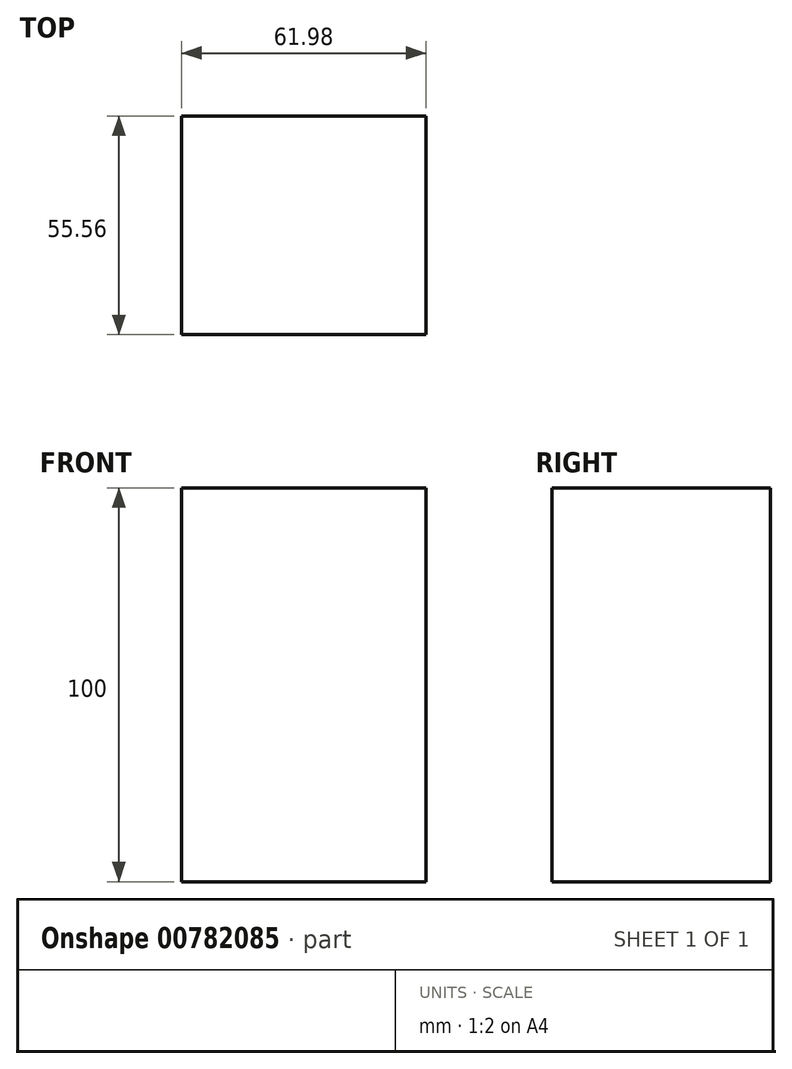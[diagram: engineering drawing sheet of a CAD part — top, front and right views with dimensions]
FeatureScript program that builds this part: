
annotation { "Feature Type Name" : "Feature", "Feature Type Description" : "" }
export const myFeature = defineFeature(function(context is Context, id is Id, definition is map)
    precondition{}
    {
        {
            var Q0;
            Q0=qCreatedBy(makeId("Top.planeOp"),FACE);
            var sketch = newSketch(context, id + "F0", { "sketchPlane" : qUnion([Q0])});
            skLineSegment(sketch, "E0.bottom", {"start": v(-31, 27.78) * mm, "end": v(31, 27.78) * mm});
            skLineSegment(sketch, "E0.top", {"start": v(-31, -27.78) * mm, "end": v(31, -27.78) * mm});
            skLineSegment(sketch, "E0.left", {"start": v(-31, 27.78) * mm, "end": v(-31, -27.78) * mm});
            skLineSegment(sketch, "E0.right", {"start": v(31, 27.78) * mm, "end": v(31, -27.78) * mm});
            skPoint(sketch, "E0.middle", {"position": v(0, 0) * mm});
            skSolve(sketch);
        }
        {
            var Q0;
            Q0 = qSketchRegion(id + "F0", true);
            extrude(context, id + "F1", {"entities" : qUnion([Q0]), "depth" : 100 * mm, "offsetDistance" : 25 * mm});
        }
        {
            var Q0;
            Q0=makeQuery(id+"F1.opExtrude","CAP_FACE",FACE,{"disambiguationData":[OSD([sQuery(id+"F0.wireOp",EDGE,"E0.bottom"),sQuery(id+"F0.wireOp",EDGE,"E0.top"),sQuery(id+"F0.wireOp",EDGE,"E0.left"),sQuery(id+"F0.wireOp",EDGE,"E0.right")])],"isStart":false});
            var sketch = newSketch(context, id + "F2", { "sketchPlane" : qUnion([Q0])});
            skLineSegment(sketch, "E1", {"start": v(31, 0) * mm, "end": v(-31, 0) * mm});
            skSolve(sketch);
        }
        {
            var Q0;
            {var subQ0=sQuery(id+"F2.wireOp",EDGE,"E1");Q0=makeQuery(id+"F2.imprint","IMPRINT",FACE,{"disambiguationData":[TD([[makeQuery(id+"F2.imprint","IMPRINT",EDGE,{"derivedFrom":subQ0}),-1.0]])]});}
            var sketch = newSketch(context, id + "F3", { "sketchPlane" : qUnion([Q0])});
            skCircle(sketch, "E2", {"center": v(0, 0) * mm, "radius": 17.01 * mm});
            skCircle(sketch, "E3.0", {"center": v(0, 0) * mm, "radius": 22.01 * mm});
            skSolve(sketch);
        }
        {
            var Q0;
            Q0=sQuery(id+"F3.wireOp",EDGE,"E2");
            var Q1;
            Q1=sQuery(id+"F3.wireOp",EDGE,"E3.0");
            extrude(context, id + "F4", {"bodyType" : ToolBodyType.SURFACE, "surfaceEntities" : qUnion([Q0, Q1]), "depth" : 200 * mm, "offsetDistance" : 25 * mm});
        }
    });
